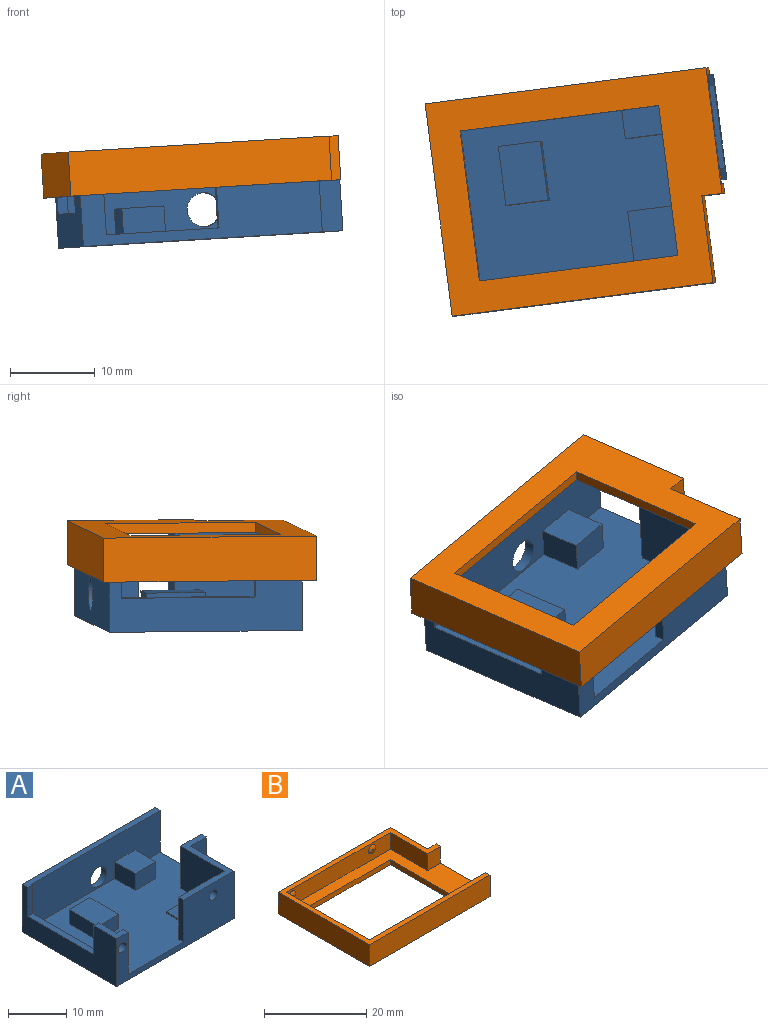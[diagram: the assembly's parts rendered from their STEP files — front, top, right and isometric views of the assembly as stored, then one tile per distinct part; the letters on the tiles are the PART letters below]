
ASSEMBLY  parts=2 mates=1
PART A: 39 faces, bbox 32.2x22.9x10 mm
  f0: plane 5.5x2.8mm, normal (0,0,1), area 8.5mm2, adj f1,f5,f8,f9,f11,f33
  f1: plane 20.5x8.8mm, normal (1,0,0), area 84.4mm2, adj f0,f2,f4,f9,f12,f31,f32,f33
  f2: plane 31x21.7mm, normal (0,0,1), area 490.1mm2, adj f1,f3,f4,f5,f6,f8,f9,f13
  f3: plane 10.5x8.8mm, normal (-1,0,0), area 90.3mm2, adj f2,f13,f14,f18,f28,f30
  f4: plane 31x8.8mm, normal (0,-1,0), area 242.7mm2, adj f1,f2,f6,f12,f24,f26,f27,f34
  f5: plane 28.4x10mm, normal (0,-1,0), area 159.8mm2, adj f0,f2,f7,f8,f11,f15,f16,f18
  f6: plane 12.4x10mm, normal (1,0,0), area 36mm2, adj f2,f4,f7,f10,f12,f13,f17,f18
  f7: plane 32.2x22.9mm, normal (0,0,-1), area 697.5mm2, adj f5,f6,f10,f11,f16,f17
  f8: plane 8.8x1.2mm, normal (1,0,0), area 10.6mm2, adj f0,f2,f5,f9
  f9: plane 8.8x1.6mm, normal (0,1,0), area 14.1mm2, adj f0,f1,f2,f8
  f10: plane 32.2x10mm, normal (0,1,0), area 303.2mm2, adj f6,f7,f11,f12,f34,f37,f38
  f11: plane 22.9x10mm, normal (-1,0,0), area 133mm2, adj f0,f5,f7,f10,f12,f31,f32,f33
  f12: plane 32.2x1.4mm, normal (0,0,1), area 38.9mm2, adj f1,f4,f6,f10,f11,f31
  f13: plane 8.8x5mm, normal (0,1,0), area 44mm2, adj f2,f3,f6,f18
  f14: plane 11x8.8mm, normal (0,1,0), area 94.7mm2, adj f2,f3,f15,f18,f29,f30
  f15: plane 8.8x1.2mm, normal (-1,0,0), area 10.6mm2, adj f2,f5,f14,f18
  f16: plane 10.5x10mm, normal (1,0,0), area 105mm2, adj f5,f7,f17,f18
  f17: plane 10x3.8mm, normal (0,-1,0), area 38mm2, adj f6,f7,f16,f18
  f18: plane 16x11.7mm, normal (0,0,1), area 31.8mm2, adj f3,f5,f6,f13,f14,f15,f16,f17
  f19: plane 5x3mm, normal (0,1,0), area 15mm2, adj f2,f20,f22,f23
  f20: plane 7x3mm, normal (-1,0,0), area 21mm2, adj f2,f19,f21,f23
  f21: plane 5x3mm, normal (0,-1,0), area 15mm2, adj f2,f20,f22,f23
  f22: plane 7x3mm, normal (1,0,0), area 21mm2, adj f2,f19,f21,f23
  f23: plane 7x5mm, normal (0,0,1), area 35mm2, adj f19,f20,f21,f22
  f24: plane 5x3.5mm, normal (-1,0,0), area 17.5mm2, adj f2,f4,f25,f27
  f25: plane 5x3.5mm, normal (0,-1,0), area 17.5mm2, adj f2,f24,f26,f27
  f26: plane 5x3.5mm, normal (1,0,0), area 17.5mm2, adj f2,f4,f25,f27
  f27: plane 5x5mm, normal (0,0,1), area 25mm2, adj f4,f24,f25,f26
  f28: plane 7x0.3mm, normal (0,1,0), area 2.1mm2, adj f2,f3,f29,f30
  f29: plane 7x0.3mm, normal (-1,0,0), area 2.1mm2, adj f2,f14,f28,f30
  f30: plane 7x7mm, normal (0,0,1), area 49mm2, adj f3,f14,f28,f29
  f31: plane 6x1.2mm, normal (0,-1,0), area 7.2mm2, adj f1,f11,f12,f32
  f32: plane 16x1.2mm, normal (0,0,1), area 19.2mm2, adj f1,f11,f31,f33
  f33: plane 6x1.2mm, normal (0,1,0), area 7.2mm2, adj f0,f1,f11,f32
  f34: cylinder r=2mm len=4mm, axis (0,1,0), area 15.1mm2, adj f4,f10
  f35: sphere r=1mm, area 6.3mm2, adj f5
  f36: sphere r=1mm, area 6.3mm2, adj f5
  f37: sphere r=1mm, area 6.3mm2, adj f10
  f38: sphere r=1mm, area 6.3mm2, adj f10
PART B: 26 faces, bbox 33.4x25.2x5.2 mm
  f0: plane 10.3x4mm, normal (-1,0,0), area 41.2mm2, adj f1,f10,f11,f13
  f1: plane 4x3.6mm, normal (0,-1,0), area 14.4mm2, adj f0,f7,f11,f13
  f2: plane 5.2x2.4mm, normal (0,1,0), area 12.5mm2, adj f3,f7,f11,f12
  f3: plane 10.3x5.2mm, normal (1,0,0), area 53.6mm2, adj f2,f4,f11,f12
  f4: plane 31x5.2mm, normal (0,1,0), area 161.2mm2, adj f3,f5,f11,f12
  f5: plane 25.2x5.2mm, normal (-1,0,0), area 131mm2, adj f4,f6,f11,f12
  f6: plane 33.4x5.2mm, normal (0,-1,0), area 173.7mm2, adj f5,f7,f11,f12
  f7: plane 14.9x5.2mm, normal (1,0,0), area 27.5mm2, adj f1,f2,f6,f8,f11,f12,f13
  f8: plane 32.2x4mm, normal (0,1,0), area 122.5mm2, adj f7,f9,f11,f13,f24,f25
  f9: plane 22.8x4mm, normal (1,0,0), area 91.2mm2, adj f8,f10,f11,f13
  f10: plane 28.6x4mm, normal (0,-1,0), area 108.1mm2, adj f0,f9,f11,f13,f20,f21
  f11: plane 33.4x25.2mm, normal (0,0,1), area 119.9mm2, adj f0,f1,f2,f3,f4,f5,f6,f7
  f12: plane 33.4x25.2mm, normal (0,0,-1), area 396.9mm2, adj f2,f3,f4,f5,f6,f7,f14,f15
  f13: plane 32.2x22.8mm, normal (0,0,1), area 277mm2, adj f0,f1,f7,f8,f9,f10,f14,f15
  f14: plane 17.8x1.2mm, normal (1,0,0), area 21.4mm2, adj f12,f13,f15,f17
  f15: plane 23.6x1.2mm, normal (0,-1,0), area 28.3mm2, adj f12,f13,f14,f16
  f16: plane 17.8x1.2mm, normal (-1,0,0), area 21.4mm2, adj f12,f13,f15,f17
  f17: plane 23.6x1.2mm, normal (0,1,0), area 28.3mm2, adj f12,f13,f14,f16
  f18: plane 0.2x0.2mm, normal (0,-1,0), area 0mm2, adj f21
  f19: plane 0.2x0.2mm, normal (0,-1,0), area 0mm2, adj f20
  f20: torus R=0.1mm, axis (0,-1,0), area 3.4mm2, adj f10,f19
  f21: torus R=0.1mm, axis (0,-1,0), area 3.4mm2, adj f10,f18
  f22: plane 0.2x0.2mm, normal (0,1,0), area 0mm2, adj f25
  f23: plane 0.2x0.2mm, normal (0,1,0), area 0mm2, adj f24
  f24: torus R=0.1mm, axis (0,1,0), area 3.4mm2, adj f8,f23
  f25: torus R=0.1mm, axis (0,1,0), area 3.4mm2, adj f8,f22
PLACE A rot(axis=(-0.04,-0.43,0.9),8.1deg) t=(-14.39,-5.24,-9.94)mm
PLACE B rot(axis=(1,0.06,0.03),179.7deg) t=(-9.3,-51.5,1.68)mm
MATE fastened A.f5 <-> B.f20  axis (0.13,-0.99,0.01) through (-28.93,-22.36,-3.29)mm
